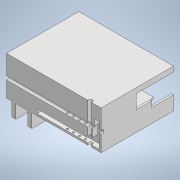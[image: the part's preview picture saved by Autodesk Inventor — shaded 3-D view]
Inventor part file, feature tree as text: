
AUTODESK INVENTOR PART (.ipt)
format: ipt  version: 2022 (Build 260153000, 153)  size: 371,200 bytes
history: native  units: in
note: dims shown in document units (in); Inventor stores cm internally (conversion verified against a paired STEP export)
features: reference x21, sketch x13, other x11, extrude x11, projected_geometry x3, plane x2, fillet x1
ambient origin geometry x8: Origin, YZ Plane, XZ Plane, XY Plane, X Axis, Y Axis, Z Axis, Center Point
bodies: Solid1 (feature_tree)
feature tree (62):
  other  "Lower Support.ipt"
  extrude  "Extrusion1"  Depth=0.3937in TaperAngle=0.0deg
  extrude  "Extrusion2"  TaperAngle=0.0deg  [1 undecoded]
  extrude  "Extrusion3"  Depth=0.0039in
  plane  "Work Plane2"
  extrude  "Extrusion4"  Depth=0.1969in
  extrude  "Extrusion7"  Depth=0.7874in
  extrude  "Extrusion8"  Depth=0.3937in
  extrude  "Extrusion12"  Depth=0.1969in
  fillet  "Fillet4"  Radius=0.1969in
  sketch  "Sketch22"  dims[d69=0.1969in d70=0.1969in]
  plane  "Work Plane3"
  extrude  "Extrusion16"  Depth=0.3937in TaperAngle=0.0deg
  extrude  "Extrusion17"  TaperAngle=0.0deg  [1 undecoded]
  extrude  "Extrusion18"  Depth=0.1969in
  extrude  "Extrusion19"  Depth=0.1969in
  other  "Solid1::Lower Support.ipt"
  other  "TaggingFeature1"
  sketch  "Sketch1"  dims[d0=0.3937in d1=0.3937in d2=0.0in]
  sketch  "Sketch4"  dims[d3=0.0in d4=0.0in d5=0.0in d6=0.0in]
  sketch  "Sketch5"  dims[d7=7.4803in d8=0.0in d14=0.0039in]
  sketch  "Sketch6"  dims[d15=0.1969in d16=0.0in d17=0.1969in]
  projected_geometry  "Projected Loop1"
  sketch  "Sketch7"  dims[d18=6.2992in d19=0.0in d39=0.7874in]
  sketch  "Sketch8"  dims[d41=0.3937in d42=0.0in d43=0.3937in]
  sketch  "Sketch9"  dims[d44=0.1969in d61=0.0039in d62=0.1969in]
  projected_geometry  "Projected Loop2"
  sketch  "Sketch13"  dims[d63=0.0039in d64=0.3937in d65=0.0in]
  reference  "Reference2"
  sketch  "Sketch14"  dims[d66=0.2323in d67=0.0in d68=0.0in]
  projected_geometry  "Projected Loop3"
  reference  "Reference25"
  reference  "Reference26"
  reference  "Reference27"
  reference  "Reference28"
  reference  "Reference29"
  sketch  "Sketch23"  dims[d71=0.1969in d72=0.1969in]
  reference  "Reference30"
  reference  "Reference31"
  sketch  "Sketch24"  dims[d73=0.1969in]
  reference  "Reference32"
  reference  "Reference33"
  reference  "Reference34"
  reference  "Reference35"
  reference  "Reference36"
  reference  "Reference37"
  reference  "Reference38"
  reference  "Reference39"
  reference  "Reference40"
  reference  "Reference41"
  reference  "Reference42"
  reference  "Reference43"
  sketch  "Sketch25"  dims[d74=0.1969in d75=0.1969in d76=0.1969in d77=0.1969in d78=0.0in d79=0.0in d80=0.0in d81=0.0in]
  reference  "Reference44"
  other  "Linear Rail Assembly.iam"
  other  "backboard_MIR:1"
  other  "linear actuator:1"
  other  "Power brick assembly:1"
  other  "IEC 320 C13 Cable End:1"
  other  "printer power brick assembly:2"
  other  "printer power brick assembly:1"
  other  "Lower Support:1"
note: 2 required parameter values undecoded (feature->parameter linkage not recoverable at this tier; creation-order binding heuristic only, values carry confidence <= 0.55)
